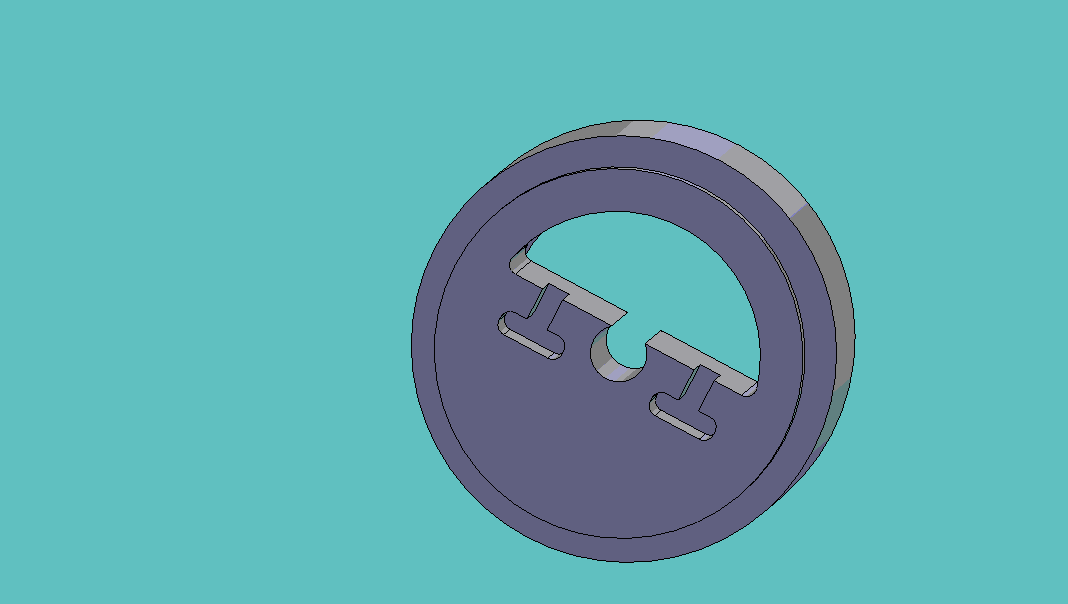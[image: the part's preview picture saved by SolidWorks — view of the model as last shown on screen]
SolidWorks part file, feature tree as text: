
SOLIDWORKS PART (.sldprt)
format: sldprt  version: not decoded by parser v0  size: 216,064 bytes
history: native  units: mm
features: plane x3, sketch x3, cut_extrude x2, material x1, revolve x1 (+13 scaffold rows collapsed)
feature tree (23):
  scaffold x13  (default folders/planes/origin — collapsed)
  material  "Matériau <non spécifié>"
  plane  "Plan de face"
  plane  "Plan de dessus"
  plane  "Plan de droite"
  sketch  "Esquisse1"  dims[c1.D1=4.0mm c1.D2=16.0mm c1.D3=6.0mm c1.D4=12.5mm c1.D5=15.0mm c1.D6=2.0mm c1.D7=2.4mm c1.D8=3.0mm c1.D9=6.4mm c1.D10=17.5mm c1.D11=6.4mm c1.D12=3.0mm c1.D13=2.4mm c1.D14=2.0mm c1.D15=22.0mm c1.D16=4.0mm c2.D5=15.0mm c2.D1=4.0mm]
  revolve  "Révolution1"  Angle=360deg
  sketch  "Esquisse2"  dims[D1=3.0mm]
  cut_extrude  "Extrusion1"  [1 undecoded]
  sketch  "Esquisse3"  dims[c1.D1=1.6mm c1.D2=1.6mm c1.D3=5.0mm c2.D1=3.5mm]
  cut_extrude  "Extrusion2"  Depth=6mm
decode coverage: 5 of 6 modeling features carry decoded parameters
note: 1 parameter value undecoded
note: suppression state not decoded; provenance and decode notes live in map.json
